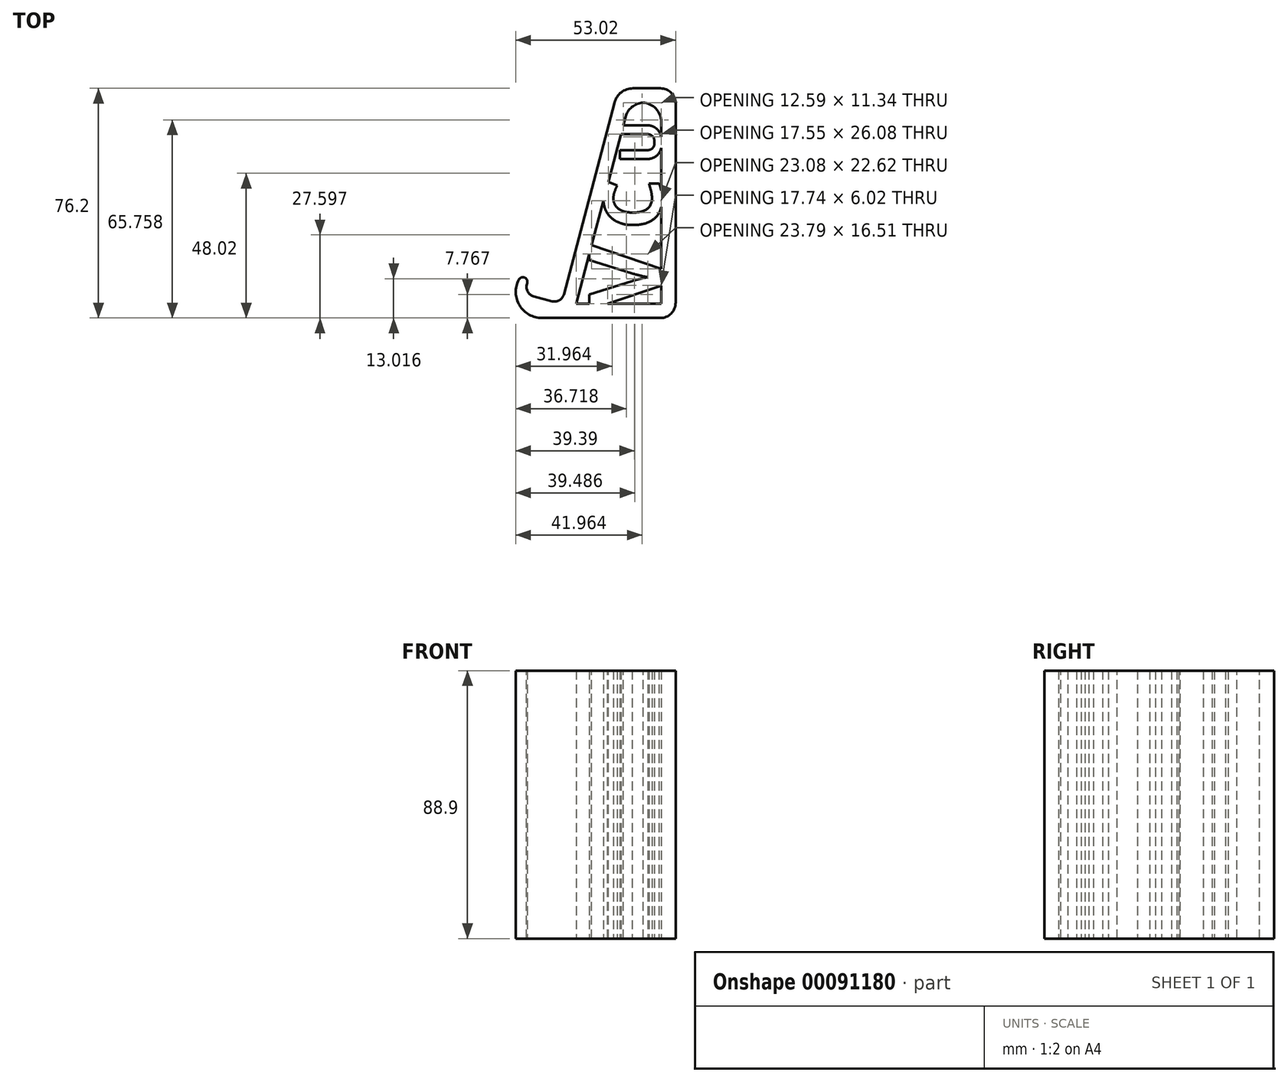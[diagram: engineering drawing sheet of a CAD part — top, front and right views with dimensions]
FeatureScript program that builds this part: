
annotation { "Feature Type Name" : "Feature", "Feature Type Description" : "" }
export const myFeature = defineFeature(function(context is Context, id is Id, definition is map)
    precondition{}
    {
        {
            var Q0;
            Q0=qCreatedBy(makeId("Top.planeOp"),FACE);
            var sketch = newSketch(context, id + "F0", { "sketchPlane" : qUnion([Q0])});
            skLineSegment(sketch, "E0.bottom", {"start": v(37.44, -49.98) * mm, "end": v(-6.9, -49.98) * mm});
            skLineSegment(sketch, "E0.left", {"start": v(37.44, -49.98) * mm, "end": v(37.44, 26.22) * mm});
            skLineSegment(sketch, "E1.0", {"start": v(37.44, 26.22) * mm, "end": v(18.4, 26.22) * mm});
            skLineSegment(sketch, "E2", {"start": v(18.4, 26.22) * mm, "end": v(-0.43, -45.22) * mm});
            skLineSegment(sketch, "E3", {"start": v(-0.43, -45.22) * mm, "end": v(-12.71, -41.99) * mm});
            skLineSegment(sketch, "E4", {"start": v(-12.71, -41.99) * mm, "end": v(-11.76, -38.38) * mm});
            skArc(sketch, "E5", {"start": v(-14.59, -37.29) * mm, "mid": v(-14.32, -45.8) * mm, "end": v(-6.9, -49.98) * mm});
            skPoint(sketch, "E6.visualSharp", {"position": v(-10.45, -33.39) * mm});
            skArc(sketch, "E6.filletArc", {"start": v(-11.76, -38.38) * mm, "mid": v(-12.69, -36.57) * mm, "end": v(-14.59, -37.29) * mm});
            skPoint(sketch, "E0.top.start.orphan", {"position": v(37.44, 67.5) * mm});
            skPoint(sketch, "E7.orphan", {"position": v(-24.48, 50.96) * mm});
            skLineSegment(sketch, "E8.0", {"start": v(22.06, 21.45) * mm, "end": v(4.5, -45.22) * mm});
            skLineSegment(sketch, "E8.1", {"start": v(32.68, 21.45) * mm, "end": v(22.06, 21.45) * mm});
            skLineSegment(sketch, "E8.2", {"start": v(32.68, -45.22) * mm, "end": v(32.68, 21.45) * mm});
            skLineSegment(sketch, "E9.0", {"start": v(32.68, -45.22) * mm, "end": v(4.5, -45.22) * mm});
            skSolve(sketch);
        }
        {
            var Q0;
            Q0=makeQuery(id+"F0.imprint","IMPRINT",FACE,{"disambiguationData":[TD([[makeQuery(id+"F0.imprint","IMPRINT",EDGE,{"derivedFrom":sQuery(id+"F0.wireOp",EDGE,"E0.bottom")}),-1.0]])]});
            extrude(context, id + "F1", {"entities" : qUnion([Q0]), "endBound" : BoundingType.SYMMETRIC, "depth" : 88.9 * mm});
        }
        {
            var Q0;
            {var subQ0=sQuery(id+"F0.wireOp",EDGE,"E4");var subQ1=sQuery(id+"F0.wireOp",EDGE,"E3");Q0=makeQuery(id+"FyOYqFq6HKQU54Y_1.boolean.opBoolean","SPLIT",EDGE,{"disambiguationData":[TD([makeQuery(id+"FyOYqFq6HKQU54Y_1.opExtrude","SWEPT_FACE",FACE,{"disambiguationData":[OSD([sQuery(id+"FY32ovTUcWpiQAg_1.wireOp",EDGE,"HsAG6LeL-DGmH-5yRH-Sm6S-k9NTCG4IdJSy.top")])]})])],"derivedFrom":makeQuery(id+"F1.opExtrude","SWEPT_EDGE",EDGE,{"disambiguationData":[OSD([subQ1,subQ0])]})});}
            var Q1;
            {var subQ0=sQuery(id+"F0.wireOp",EDGE,"E4");var subQ1=sQuery(id+"F0.wireOp",EDGE,"E3");Q1=makeQuery(id+"FyOYqFq6HKQU54Y_1.boolean.opBoolean","SPLIT",EDGE,{"disambiguationData":[TD([makeQuery(id+"FyOYqFq6HKQU54Y_1.opExtrude","SWEPT_FACE",FACE,{"disambiguationData":[OSD([sQuery(id+"FY32ovTUcWpiQAg_1.wireOp",EDGE,"HsAG6LeL-DGmH-5yRH-Sm6S-k9NTCG4IdJSy.bottom")])]})])],"derivedFrom":makeQuery(id+"F1.opExtrude","SWEPT_EDGE",EDGE,{"disambiguationData":[OSD([subQ1,subQ0])]})});}
            var Q2;
            {var subQ0=sQuery(id+"F0.wireOp",EDGE,"E2");var subQ1=sQuery(id+"F0.wireOp",EDGE,"E3");Q2=makeQuery(id+"FyOYqFq6HKQU54Y_1.boolean.opBoolean","SPLIT",EDGE,{"disambiguationData":[TD([makeQuery(id+"FyOYqFq6HKQU54Y_1.opExtrude","SWEPT_FACE",FACE,{"disambiguationData":[OSD([sQuery(id+"FY32ovTUcWpiQAg_1.wireOp",EDGE,"HsAG6LeL-DGmH-5yRH-Sm6S-k9NTCG4IdJSy.top")])]})])],"derivedFrom":makeQuery(id+"F1.opExtrude","SWEPT_EDGE",EDGE,{"disambiguationData":[OSD([subQ0,subQ1])]})});}
            var Q3;
            {var subQ0=sQuery(id+"F0.wireOp",EDGE,"E3");var subQ1=sQuery(id+"F0.wireOp",EDGE,"E2");Q3=makeQuery(id+"FyOYqFq6HKQU54Y_1.boolean.opBoolean","SPLIT",EDGE,{"disambiguationData":[TD([makeQuery(id+"FyOYqFq6HKQU54Y_1.opExtrude","SWEPT_FACE",FACE,{"disambiguationData":[OSD([sQuery(id+"FY32ovTUcWpiQAg_1.wireOp",EDGE,"HsAG6LeL-DGmH-5yRH-Sm6S-k9NTCG4IdJSy.bottom")])]})])],"derivedFrom":makeQuery(id+"F1.opExtrude","SWEPT_EDGE",EDGE,{"disambiguationData":[OSD([subQ1,subQ0])]})});}
            fillet(context, id + "F2", {"entities" : qUnion([Q0, Q1, Q2, Q3]), "radius" : 3.17 * mm, "tangentPropagation" : true, "allowEdgeOverflow" : false});
        }
        {
            var Q0;
            {var subQ0=sQuery(id+"F0.wireOp",EDGE,"E0.left");var subQ1=sQuery(id+"F0.wireOp",EDGE,"E0.bottom");Q0=makeQuery(id+"FhLXFpEwqwEHnt2_1.boolean.opBoolean","SPLIT",EDGE,{"disambiguationData":[TD([makeQuery(id+"FyOYqFq6HKQU54Y_1.boolean.opBoolean","COPY",FACE,{"derivedFrom":makeQuery(id+"FyOYqFq6HKQU54Y_1.opExtrude","SWEPT_FACE",FACE,{"disambiguationData":[OSD([sQuery(id+"FY32ovTUcWpiQAg_1.wireOp",EDGE,"HsAG6LeL-DGmH-5yRH-Sm6S-k9NTCG4IdJSy.top")])]})})])],"derivedFrom":makeQuery(id+"F1.opExtrude","SWEPT_EDGE",EDGE,{"disambiguationData":[OSD([subQ1,subQ0])]})});}
            var Q1;
            {var subQ0=sQuery(id+"F0.wireOp",EDGE,"E0.left");var subQ1=sQuery(id+"F0.wireOp",EDGE,"E0.bottom");Q1=makeQuery(id+"FhLXFpEwqwEHnt2_1.boolean.opBoolean","SPLIT",EDGE,{"disambiguationData":[TD([makeQuery(id+"FyOYqFq6HKQU54Y_1.boolean.opBoolean","COPY",FACE,{"derivedFrom":makeQuery(id+"FyOYqFq6HKQU54Y_1.opExtrude","SWEPT_FACE",FACE,{"disambiguationData":[OSD([sQuery(id+"FY32ovTUcWpiQAg_1.wireOp",EDGE,"HsAG6LeL-DGmH-5yRH-Sm6S-k9NTCG4IdJSy.bottom")])]})})])],"derivedFrom":makeQuery(id+"F1.opExtrude","SWEPT_EDGE",EDGE,{"disambiguationData":[OSD([subQ1,subQ0])]})});}
            var Q2;
            Q2=makeQuery(id+"F1.opExtrude","SWEPT_EDGE",EDGE,{"disambiguationData":[OSD([sQuery(id+"F0.wireOp",EDGE,"E0.left"),sQuery(id+"F0.wireOp",EDGE,"E1.0")])]});
            fillet(context, id + "F3", {"entities" : qUnion([Q0, Q1, Q2]), "radius" : 5.08 * mm, "tangentPropagation" : true, "allowEdgeOverflow" : false});
        }
        {
            var Q0;
            Q0=makeQuery(id+"F1.opExtrude","SWEPT_EDGE",EDGE,{"disambiguationData":[OSD([sQuery(id+"F0.wireOp",EDGE,"E1.0"),sQuery(id+"F0.wireOp",EDGE,"E2")])]});
            fillet(context, id + "F4", {"entities" : qUnion([Q0]), "radius" : 6.35 * mm, "tangentPropagation" : true, "allowEdgeOverflow" : false});
        }
        {
            var Q0;
            Q0=makeQuery(id+"F1.opExtrude","SWEPT_EDGE",EDGE,{"disambiguationData":[OSD([sQuery(id+"F0.wireOp",EDGE,"E8.0"),sQuery(id+"F0.wireOp",EDGE,"E8.1")])]});
            var Q1;
            Q1=makeQuery(id+"F1.opExtrude","SWEPT_EDGE",EDGE,{"disambiguationData":[OSD([sQuery(id+"F0.wireOp",EDGE,"E8.1"),sQuery(id+"F0.wireOp",EDGE,"E8.2")])]});
            fillet(context, id + "F5", {"entities" : qUnion([Q0, Q1]), "radius" : 6.35 * mm, "tangentPropagation" : true, "allowEdgeOverflow" : false});
        }
        {
            var Q0;
            Q0=qCreatedBy(makeId("Top.planeOp"),FACE);
            var sketch = newSketch(context, id + "F6", { "sketchPlane" : qUnion([Q0])});
            skText(sketch, "E10", { "text": "V", "fontName": "OpenSans-Bold.ttf"});
            skText(sketch, "E11", { "text": "C", "fontName": "OpenSans-Bold.ttf"});
            skText(sketch, "E12", { "text": "U", "fontName": "OpenSans-Bold.ttf"});
            const initialGuessF6  = {"E10": [0.03268, -0.04729, 0, 1, 0.02404], "E11": [0.03268, -0.02068, 0, 1, 0.01911], "E12": [0.03268, 0.00113, 0, 1, 0.01378]};
            skSetInitialGuess(sketch, initialGuessF6);
            skSolve(sketch);
        }
        {
            var Q0;
            Q0 = qSketchRegion(id + "F6", true);
            extrude(context, id + "F7", {"entities" : qUnion([Q0]), "operationType" : NewBodyOperationType.ADD, "endBound" : BoundingType.SYMMETRIC, "depth" : 88.9 * mm});
        }
    });
